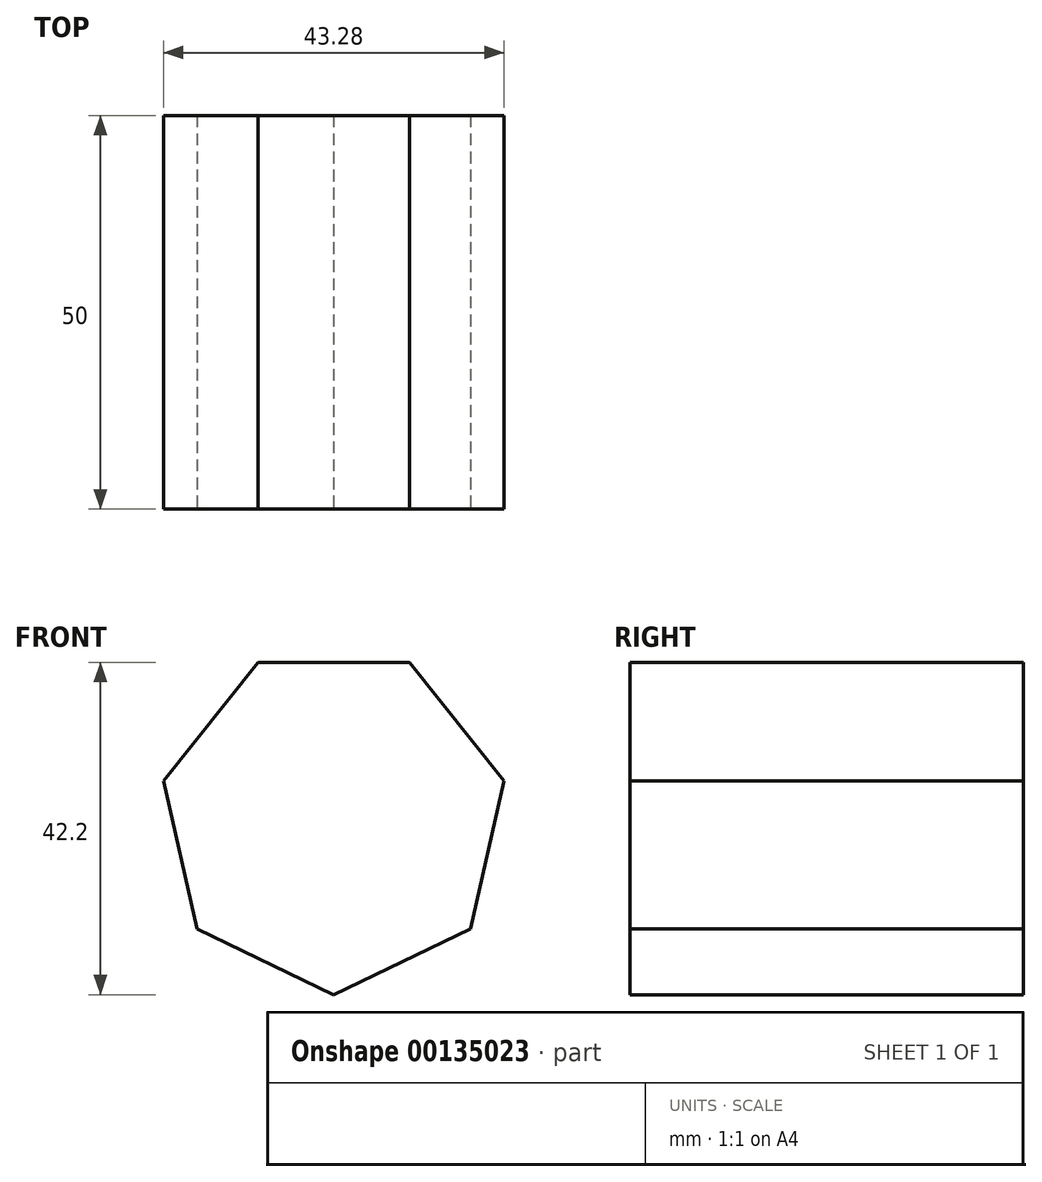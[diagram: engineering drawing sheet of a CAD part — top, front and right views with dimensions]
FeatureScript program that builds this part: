
annotation { "Feature Type Name" : "Feature", "Feature Type Description" : "" }
export const myFeature = defineFeature(function(context is Context, id is Id, definition is map)
    precondition{}
    {
        {
            var Q0;
            Q0=qCreatedBy(makeId("Front.planeOp"),FACE);
            var sketch = newSketch(context, id + "F0", { "sketchPlane" : qUnion([Q0])});
            skCircle(sketch, "E0.cCircle", {"center": v(0, 0) * mm, "radius": 20 * mm, "construction": true});
            skLineSegment(sketch, "E0.0", {"start": v(-9.63, 20) * mm, "end": v(9.63, 20) * mm});
            skLineSegment(sketch, "E0.1", {"start": v(9.63, 20) * mm, "end": v(21.64, 4.94) * mm});
            skLineSegment(sketch, "E0.2", {"start": v(21.64, 4.94) * mm, "end": v(17.36, -13.84) * mm});
            skLineSegment(sketch, "E0.3", {"start": v(17.36, -13.84) * mm, "end": v(0, -22.2) * mm});
            skLineSegment(sketch, "E0.4", {"start": v(0, -22.2) * mm, "end": v(-17.36, -13.84) * mm});
            skLineSegment(sketch, "E0.5", {"start": v(-17.36, -13.84) * mm, "end": v(-21.64, 4.94) * mm});
            skLineSegment(sketch, "E0.6", {"start": v(-21.64, 4.94) * mm, "end": v(-9.63, 20) * mm});
            skPoint(sketch, "E0.0.midPoint", {"position": v(0, 20) * mm});
            skCircle(sketch, "E1", {"center": v(0, 0) * mm, "radius": 2.5 * mm});
            skSolve(sketch);
        }
        {
            var Q0;
            Q0=makeQuery(id+"F0.imprint","IMPRINT",FACE,{"disambiguationData":[TD([[makeQuery(id+"F0.imprint","IMPRINT",EDGE,{"derivedFrom":sQuery(id+"F0.wireOp",EDGE,"E0.0")}),-1.0]])]});
            var Q1;
            Q1=makeQuery(id+"F0.imprint","IMPRINT",FACE,{"disambiguationData":[TD([[makeQuery(id+"F0.imprint","IMPRINT",EDGE,{"derivedFrom":sQuery(id+"F0.wireOp",EDGE,"E1")}),1.0]])]});
            var Q2;
            Q2=sQuery(id+"F0.wireOp",EDGE,"E0.4");
            var Q3;
            Q3=sQuery(id+"F0.wireOp",EDGE,"E0.5");
            var Q4;
            Q4=sQuery(id+"F0.wireOp",EDGE,"E0.6");
            var Q5;
            Q5=sQuery(id+"F0.wireOp",EDGE,"E0.0");
            var Q6;
            Q6=sQuery(id+"F0.wireOp",EDGE,"E1");
            var Q7;
            Q7=sQuery(id+"F0.wireOp",EDGE,"E0.1");
            var Q8;
            Q8=sQuery(id+"F0.wireOp",EDGE,"E0.2");
            var Q9;
            Q9=sQuery(id+"F0.wireOp",EDGE,"E0.3");
            extrude(context, id + "F1", {"entities" : qUnion([Q0, Q1]), "surfaceEntities" : qUnion([Q2, Q3, Q4, Q5, Q6, Q7, Q8, Q9]), "endBound" : BoundingType.SYMMETRIC, "oppositeDirection" : true, "depth" : 50 * mm});
        }
    });
